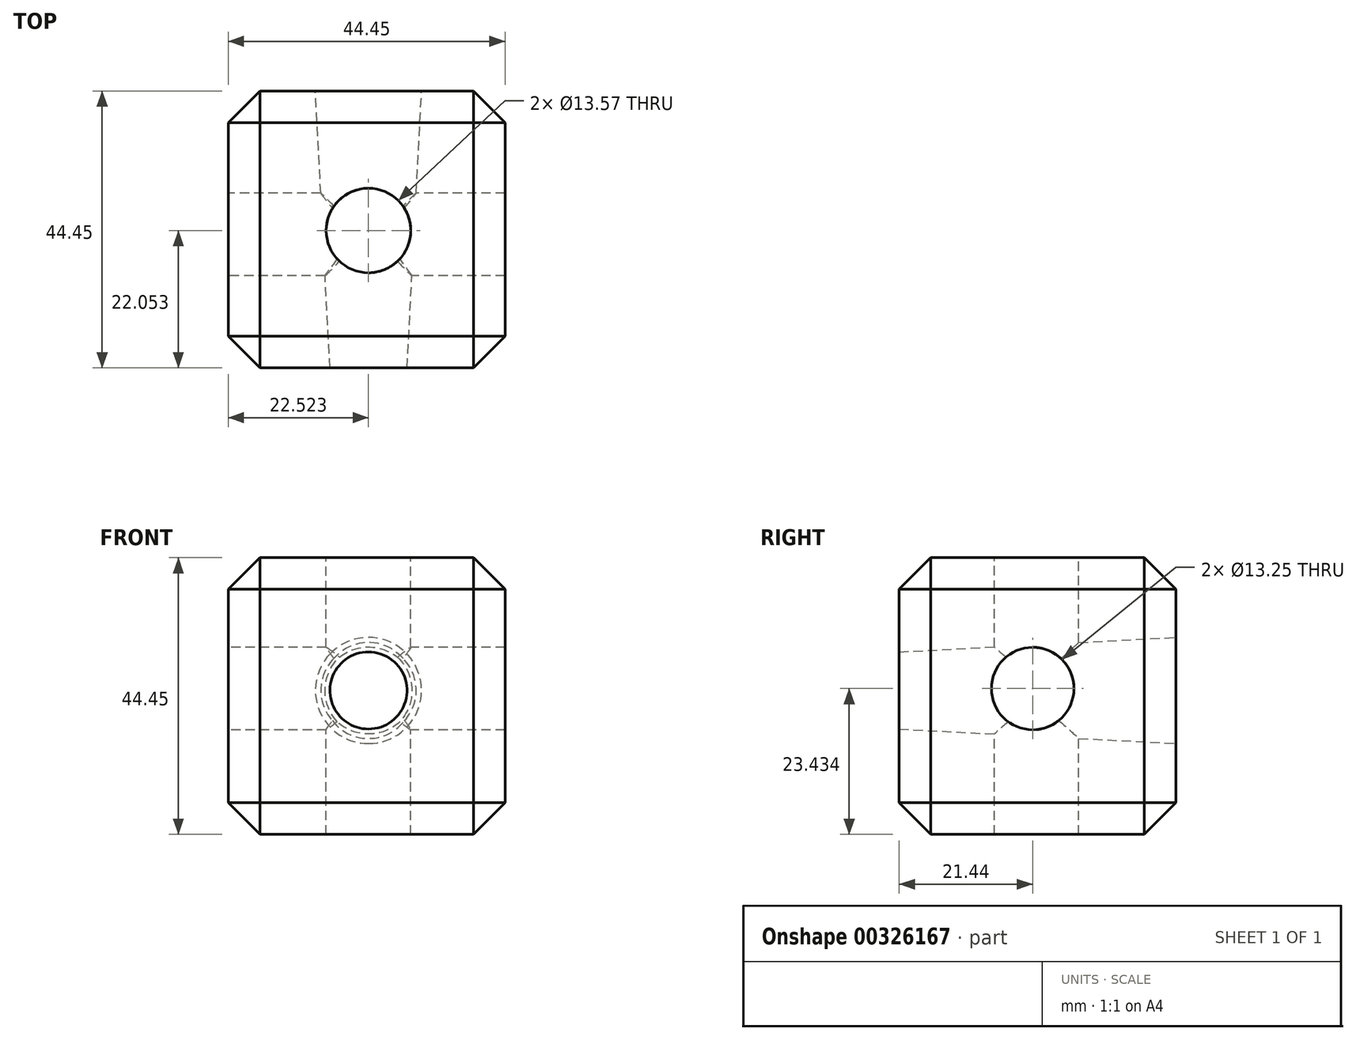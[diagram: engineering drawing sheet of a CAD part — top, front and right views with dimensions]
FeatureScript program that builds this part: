
annotation { "Feature Type Name" : "Feature", "Feature Type Description" : "" }
export const myFeature = defineFeature(function(context is Context, id is Id, definition is map)
    precondition{}
    {
        {
            var Q0;
            Q0=qCreatedBy(makeId("Front.planeOp"),FACE);
            var sketch = newSketch(context, id + "F0", { "sketchPlane" : qUnion([Q0])});
            skLineSegment(sketch, "E0.bottom", {"start": v(-59.67, 44.94) * mm, "end": v(-15.22, 44.94) * mm});
            skLineSegment(sketch, "E0.top", {"start": v(-59.67, 0.49) * mm, "end": v(-15.22, 0.49) * mm});
            skLineSegment(sketch, "E0.left", {"start": v(-59.67, 44.94) * mm, "end": v(-59.67, 0.49) * mm});
            skLineSegment(sketch, "E0.right", {"start": v(-15.22, 44.94) * mm, "end": v(-15.22, 0.49) * mm});
            skSolve(sketch);
        }
        {
            var Q0;
            Q0=makeQuery(id+"F0.imprint","IMPRINT",FACE,{"disambiguationData":[TD([[makeQuery(id+"F0.imprint","IMPRINT",EDGE,{"derivedFrom":sQuery(id+"F0.wireOp",EDGE,"E0.bottom")}),-1.0]])]});
            extrude(context, id + "F1", {"entities" : qUnion([Q0]), "depth" : 44.45 * mm, "offsetDistance" : 25.4 * mm});
        }
        {
            var Q0;
            Q0=makeQuery(id+"F1.opExtrude","CAP_EDGE",EDGE,{"disambiguationData":[OSD([sQuery(id+"F0.wireOp",EDGE,"E0.bottom")])],"isStart":false});
            var Q1;
            Q1=makeQuery(id+"F1.opExtrude","CAP_EDGE",EDGE,{"disambiguationData":[OSD([sQuery(id+"F0.wireOp",EDGE,"E0.left")])],"isStart":false});
            var Q2;
            Q2=makeQuery(id+"F1.opExtrude","CAP_EDGE",EDGE,{"disambiguationData":[OSD([sQuery(id+"F0.wireOp",EDGE,"E0.top")])],"isStart":false});
            var Q3;
            Q3=makeQuery(id+"F1.opExtrude","CAP_EDGE",EDGE,{"disambiguationData":[OSD([sQuery(id+"F0.wireOp",EDGE,"E0.right")])],"isStart":false});
            var Q4;
            Q4=makeQuery(id+"F1.opExtrude","SWEPT_EDGE",EDGE,{"disambiguationData":[OSD([sQuery(id+"F0.wireOp",EDGE,"E0.bottom"),sQuery(id+"F0.wireOp",EDGE,"E0.right")])]});
            var Q5;
            Q5=makeQuery(id+"F1.opExtrude","CAP_EDGE",EDGE,{"disambiguationData":[OSD([sQuery(id+"F0.wireOp",EDGE,"E0.bottom")])],"isStart":true});
            var Q6;
            Q6=makeQuery(id+"F1.opExtrude","SWEPT_EDGE",EDGE,{"disambiguationData":[OSD([sQuery(id+"F0.wireOp",EDGE,"E0.bottom"),sQuery(id+"F0.wireOp",EDGE,"E0.left")])]});
            var Q7;
            Q7=makeQuery(id+"F1.opExtrude","SWEPT_EDGE",EDGE,{"disambiguationData":[OSD([sQuery(id+"F0.wireOp",EDGE,"E0.top"),sQuery(id+"F0.wireOp",EDGE,"E0.right")])]});
            var Q8;
            Q8=makeQuery(id+"F1.opExtrude","CAP_EDGE",EDGE,{"disambiguationData":[OSD([sQuery(id+"F0.wireOp",EDGE,"E0.top")])],"isStart":true});
            var Q9;
            Q9=makeQuery(id+"F1.opExtrude","SWEPT_EDGE",EDGE,{"disambiguationData":[OSD([sQuery(id+"F0.wireOp",EDGE,"E0.top"),sQuery(id+"F0.wireOp",EDGE,"E0.left")])]});
            var Q10;
            Q10=makeQuery(id+"F1.opExtrude","CAP_EDGE",EDGE,{"disambiguationData":[OSD([sQuery(id+"F0.wireOp",EDGE,"E0.right")])],"isStart":true});
            var Q11;
            Q11=makeQuery(id+"F1.opExtrude","CAP_EDGE",EDGE,{"disambiguationData":[OSD([sQuery(id+"F0.wireOp",EDGE,"E0.left")])],"isStart":true});
            var Q12;
            Q12=makeQuery(id+"F1.opExtrude","SWEPT_FACE",FACE,{"disambiguationData":[OSD([sQuery(id+"F0.wireOp",EDGE,"E0.right")])]});
            chamfer(context, id + "F2", {"entities" : qUnion([Q0, Q1, Q2, Q3, Q4, Q5, Q6, Q7, Q8, Q9, Q10, Q11, Q12]), "width" : 5.08 * mm, "tangentPropagation" : true});
        }
        {
            var Q0;
            Q0=makeQuery(id+"F1.opExtrude","CAP_FACE",FACE,{"disambiguationData":[OSD([sQuery(id+"F0.wireOp",EDGE,"E0.bottom"),sQuery(id+"F0.wireOp",EDGE,"E0.top"),sQuery(id+"F0.wireOp",EDGE,"E0.left"),sQuery(id+"F0.wireOp",EDGE,"E0.right")])],"isStart":false});
            var sketch = newSketch(context, id + "F3", { "sketchPlane" : qUnion([Q0])});
            skCircle(sketch, "E1", {"center": v(-37.15, 23.61) * mm, "radius": 6.2 * mm});
            skSolve(sketch);
        }
        {
            var Q0;
            Q0=makeQuery(id+"F3.imprint","IMPRINT",FACE,{"disambiguationData":[TD([[makeQuery(id+"F3.imprint","IMPRINT",EDGE,{"derivedFrom":sQuery(id+"F3.wireOp",EDGE,"E1")}),1.0]])]});
            extrude(context, id + "F4", {"entities" : qUnion([Q0]), "operationType" : NewBodyOperationType.REMOVE, "oppositeDirection" : true, "depth" : 44.45 * mm, "offsetDistance" : 25.4 * mm, "hasDraft" : true, "draftAngle" : 3 * degree});
        }
        {
            var Q0;
            Q0=makeQuery(id+"F1.opExtrude","SWEPT_FACE",FACE,{"disambiguationData":[OSD([sQuery(id+"F0.wireOp",EDGE,"E0.left")])]});
            var sketch = newSketch(context, id + "F5", { "sketchPlane" : qUnion([Q0])});
            skCircle(sketch, "E2", {"center": v(23.01, 23.92) * mm, "radius": 6.62 * mm});
            skSolve(sketch);
        }
        {
            var Q0;
            Q0=makeQuery(id+"F5.imprint","IMPRINT",FACE,{"disambiguationData":[TD([[makeQuery(id+"F5.imprint","IMPRINT",EDGE,{"derivedFrom":sQuery(id+"F5.wireOp",EDGE,"E2")}),1.0]])]});
            extrude(context, id + "F6", {"entities" : qUnion([Q0]), "operationType" : NewBodyOperationType.REMOVE, "oppositeDirection" : true, "depth" : 44.45 * mm, "offsetDistance" : 25.4 * mm});
        }
        {
            var Q0;
            Q0=makeQuery(id+"F1.opExtrude","SWEPT_FACE",FACE,{"disambiguationData":[OSD([sQuery(id+"F0.wireOp",EDGE,"E0.bottom")])]});
            var sketch = newSketch(context, id + "F7", { "sketchPlane" : qUnion([Q0])});
            skCircle(sketch, "E3", {"center": v(-37.15, -22.4) * mm, "radius": 6.79 * mm});
            skSolve(sketch);
        }
        {
            var Q0;
            Q0 = qSketchRegion(id + "F7", true);
            extrude(context, id + "F8", {"entities" : qUnion([Q0]), "operationType" : NewBodyOperationType.REMOVE, "oppositeDirection" : true, "depth" : 44.45 * mm, "offsetDistance" : 25.4 * mm});
        }
    });
